# Revit family: 306_a2c13782d9fd4831af0d532128a45b
name_source: partatom
category: Pipe Accessories
revit_build: Autodesk Revit 2018 (Build: 20170223_1515(x64)
units: mm (PartAtom-declared; Revit-internal decimal feet)

## family parameters
Always vertical = Yes
Cut with Voids When Loaded = No
Part Type = Valve - Breaks Into
Round Connector Dimension = Use Diameter
Shared = No
Work Plane-Based = No

## types (6) — shared parameters
D5 = 20 mm  [stored 0.0656168 ft]
D6 = 21 mm
D7 = 18 mm  [stored 0.0590551 ft]
Description = Backflow preventer BA In-line 6610
L2D_Min = 3048 mm
Manufacturer = SYR
QmdConnectorList = 301;D;302;D
magiPartTypeId = 306
magiProductFamilyId = a2c13782d9fd4831af0d532128a45b

## per-type parameters (varying)
- SYR-BA-IN-LINE-6610-15: CenSd_SW1_6=13 mm; D=15 mm; D2=8 mm  [stored 0.0262467 ft]; D3=13 mm; D4=10 mm  [stored 0.0328084 ft]; H3=28 mm; H3__ve=-28 mm  [stored -0.0918635 ft]; H4=14 mm  [stored 0.0459318 ft]; H4__ve=-14 mm  [stored -0.0459318 ft]; H5=42 mm; H5__ve=-42 mm  [stored -0.137795 ft]; H6=22 mm; H6__ve=-22 mm; H7=7 mm  [stored 0.0229659 ft]; H8=15 mm  [stored 0.0492126 ft]; H8__ve=-15 mm  [stored -0.0492126 ft]; H9=43 mm; L1=101 mm; L10=4 mm  [stored 0.0131234 ft]; L2D=201 mm; L3=15 mm  [stored 0.0492126 ft]; L3__ve=-15 mm  [stored -0.0492126 ft]; L4=5 mm  [stored 0.0164042 ft]; L4__ve=-5 mm  [stored -0.0164042 ft]; L5=10 mm  [stored 0.0328084 ft]; L5__ve=-10 mm  [stored -0.0328084 ft]; L6=101 mm; L7=5 mm  [stored 0.0164042 ft]; L9=16 mm; SW1=15 mm  [stored 0.0492126 ft]; W2D=15 mm  [stored 0.0492126 ft]; magiProductId=28fcc9b5738b4ea899aa1578358918
- SYR-BA-IN-LINE-6610-50: CenSd_SW1_6=28 mm; D=50 mm; D2=25 mm; D3=30 mm; D4=28 mm; H3=39 mm; H3__ve=-39 mm; H4=20 mm  [stored 0.0656168 ft]; H4__ve=-20 mm  [stored -0.0656168 ft]; H5=59 mm; H5__ve=-59 mm; H6=25 mm; H6__ve=-25 mm; H7=8 mm  [stored 0.0262467 ft]; H8=17 mm; H8__ve=-17 mm; H9=56 mm; L1=188 mm; L10=8 mm  [stored 0.0262467 ft]; L2D=375 mm; L3=28 mm; L3__ve=-28 mm  [stored -0.0918635 ft]; L4=9 mm  [stored 0.0295276 ft]; L4__ve=-9 mm  [stored -0.0295276 ft]; L5=19 mm; L5__ve=-19 mm; L6=188 mm; L7=9 mm  [stored 0.0295276 ft]; L9=25 mm; SW1=33 mm; W2D=50 mm; magiProductId=27cf2e5b6e024cbd81009679626429
- SYR-BA-IN-LINE-6610-40: CenSd_SW1_6=24 mm; D=40 mm; D2=20 mm  [stored 0.0656168 ft]; D3=25 mm; D4=23 mm; H3=39 mm; H3__ve=-39 mm; H4=20 mm  [stored 0.0656168 ft]; H4__ve=-20 mm  [stored -0.0656168 ft]; H5=59 mm; H5__ve=-59 mm; H6=25 mm; H6__ve=-25 mm; H7=8 mm  [stored 0.0262467 ft]; H8=17 mm; H8__ve=-17 mm; H9=56 mm; L1=170 mm; L10=8 mm  [stored 0.0262467 ft]; L2D=340 mm; L3=26 mm; L3__ve=-26 mm; L4=9 mm  [stored 0.0295276 ft]; L4__ve=-9 mm  [stored -0.0295276 ft]; L5=17 mm; L5__ve=-17 mm; L6=170 mm; L7=9 mm  [stored 0.0295276 ft]; L9=23 mm; SW1=28 mm; W2D=40 mm; magiProductId=e19ecb45b74846c0bde9c63314d066
- SYR-BA-IN-LINE-6610-32: CenSd_SW1_6=20 mm  [stored 0.0656168 ft]; D=32 mm; D2=16 mm; D3=21 mm; D4=19 mm; H3=39 mm; H3__ve=-39 mm; H4=20 mm  [stored 0.0656168 ft]; H4__ve=-20 mm  [stored -0.0656168 ft]; H5=59 mm; H5__ve=-59 mm; H6=25 mm; H6__ve=-25 mm; H7=8 mm  [stored 0.0262467 ft]; H8=17 mm; H8__ve=-17 mm; H9=56 mm; L1=163 mm; L10=7 mm  [stored 0.0229659 ft]; L2D=325 mm; L3=24 mm; L3__ve=-24 mm; L4=8 mm  [stored 0.0262467 ft]; L4__ve=-8 mm; L5=16 mm; L5__ve=-16 mm; L6=163 mm; L7=8 mm  [stored 0.0262467 ft]; L9=22 mm; SW1=24 mm; W2D=32 mm; magiProductId=57ffcb5b045348ea8b678a8a69ede8
- SYR-BA-IN-LINE-6610-25: CenSd_SW1_6=17 mm; D=25 mm; D2=13 mm; D3=18 mm  [stored 0.0590551 ft]; D4=15 mm  [stored 0.0492126 ft]; H3=32 mm; H3__ve=-32 mm; H4=16 mm; H4__ve=-16 mm; H5=47 mm; H5__ve=-47 mm; H6=21 mm; H6__ve=-21 mm  [stored -0.0688976 ft]; H7=7 mm  [stored 0.0229659 ft]; H8=14 mm  [stored 0.0459318 ft]; H8__ve=-14 mm  [stored -0.0459318 ft]; H9=46 mm; L1=124 mm; L10=5 mm  [stored 0.0164042 ft]; L2D=248 mm; L3=19 mm; L3__ve=-19 mm; L4=6 mm  [stored 0.019685 ft]; L4__ve=-6 mm; L5=12 mm  [stored 0.0393701 ft]; L5__ve=-12 mm; L6=124 mm; L7=6 mm  [stored 0.019685 ft]; L9=18 mm  [stored 0.0590551 ft]; SW1=20 mm  [stored 0.0656168 ft]; W2D=25 mm; magiProductId=1c5a4d9ce6024a3885e6b8e3c01438
- SYR-BA-IN-LINE-6610-20: CenSd_SW1_6=15 mm  [stored 0.0492126 ft]; D=20 mm; D2=10 mm  [stored 0.0328084 ft]; D3=15 mm  [stored 0.0492126 ft]; D4=13 mm; H3=32 mm; H3__ve=-32 mm; H4=16 mm; H4__ve=-16 mm; H5=47 mm; H5__ve=-47 mm; H6=21 mm; H6__ve=-21 mm  [stored -0.0688976 ft]; H7=7 mm  [stored 0.0229659 ft]; H8=14 mm  [stored 0.0459318 ft]; H8__ve=-14 mm  [stored -0.0459318 ft]; H9=46 mm; L1=120 mm; L10=5 mm  [stored 0.0164042 ft]; L2D=240 mm; L3=18 mm  [stored 0.0590551 ft]; L3__ve=-18 mm  [stored -0.0590551 ft]; L4=6 mm  [stored 0.019685 ft]; L4__ve=-6 mm; L5=12 mm  [stored 0.0393701 ft]; L5__ve=-12 mm; L6=120 mm; L7=6 mm  [stored 0.019685 ft]; L9=18 mm  [stored 0.0590551 ft]; SW1=18 mm  [stored 0.0590551 ft]; W2D=20 mm  [stored 0.0656168 ft]; magiProductId=783397baa5fb4e6496fa7a04c90a31

note: column(s) folded — value = type name in every type: MC Product Code

note: [stored X ft] marks values corroborated as IEEE doubles in the binary element streams (Revit-internal decimal feet)

## geometry (parser evidence)
native form markers: Sweep x2
no freeform markers — native parametric forms only
